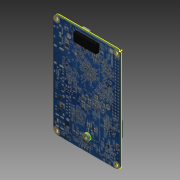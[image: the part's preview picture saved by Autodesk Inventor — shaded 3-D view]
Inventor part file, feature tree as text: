
AUTODESK INVENTOR PART (.ipt)
format: ipt  version: 2013 SP2 (Build 170200200, 200)  size: 349,184 bytes
history: native  units: mm
features: extrude x9, sketch x9, hole x2, fillet x1
ambient origin geometry x8: Origin, YZ Plane, XZ Plane, XY Plane, X Axis, Y Axis, Z Axis, Center Point
bodies: Solid1 (feature_tree)
feature tree (21):
  extrude  "Extrusion1"  Depth=100.0mm
  fillet  "Fillet1"  Radius=1.8mm
  hole  "Hole1"  [1 undecoded]
  sketch  "Sketch3"  dims[d6=0.8mm d7=0.8mm]
  extrude  "Extrusion2"  Depth=0.8mm
  extrude  "Extrusion3"  Depth=0.8mm
  extrude  "Extrusion4"  Depth=0.8mm
  extrude  "Extrusion5"  Depth=0.8mm
  sketch  "Sketch4"  dims[d8=0.8mm d9=0.8mm]
  extrude  "Extrusion6"  Depth=1.0mm TaperAngle=0.0deg
  extrude  "Extrusion7"  Depth=1.0mm TaperAngle=0.0deg
  extrude  "Extrusion8"  Depth=8.0mm TaperAngle=0.0deg
  hole  "Hole2"  [1 undecoded]
  extrude  "Extrusion9"  Depth=2.0mm TaperAngle=0.0deg
  sketch  "Sketch1"  dims[d0=64.0mm d1=100.0mm d2=1.8mm d3=0.0mm]
  sketch  "Sketch2"  dims[d4=4.0mm d5=4.0mm]
  sketch  "Sketch5"  dims[d10=0.8mm d11=0.8mm]
  sketch  "Sketch7"  dims[d12=0.8mm d13=0.8mm]
  sketch  "Sketch8"  dims[d14=3.2mm d15=6.0mm d16=4.0mm d17=2.0mm d18=90.0deg d19=8.0mm d20=20.594885mm d21=1.0mm d22=0.0mm]
  sketch  "Sketch9"  dims[d23=3.0mm d24=0.0mm d25=1.0mm d26=0.0mm]
  sketch  "Sketch10"  dims[d27=3.0mm d28=0.0mm d29=8.0mm d30=0.0mm d31=3.0mm d32=0.0mm d33=2.0mm d34=0.0mm d35=3.2mm d36=6.0mm d37=4.0mm d38=2.0mm d39=90.0deg d40=8.0mm d41=20.594885mm d42=1.0mm d43=0.0mm]
note: 2 required parameter values undecoded (feature->parameter linkage not recoverable at this tier; creation-order binding heuristic only, values carry confidence <= 0.55)
